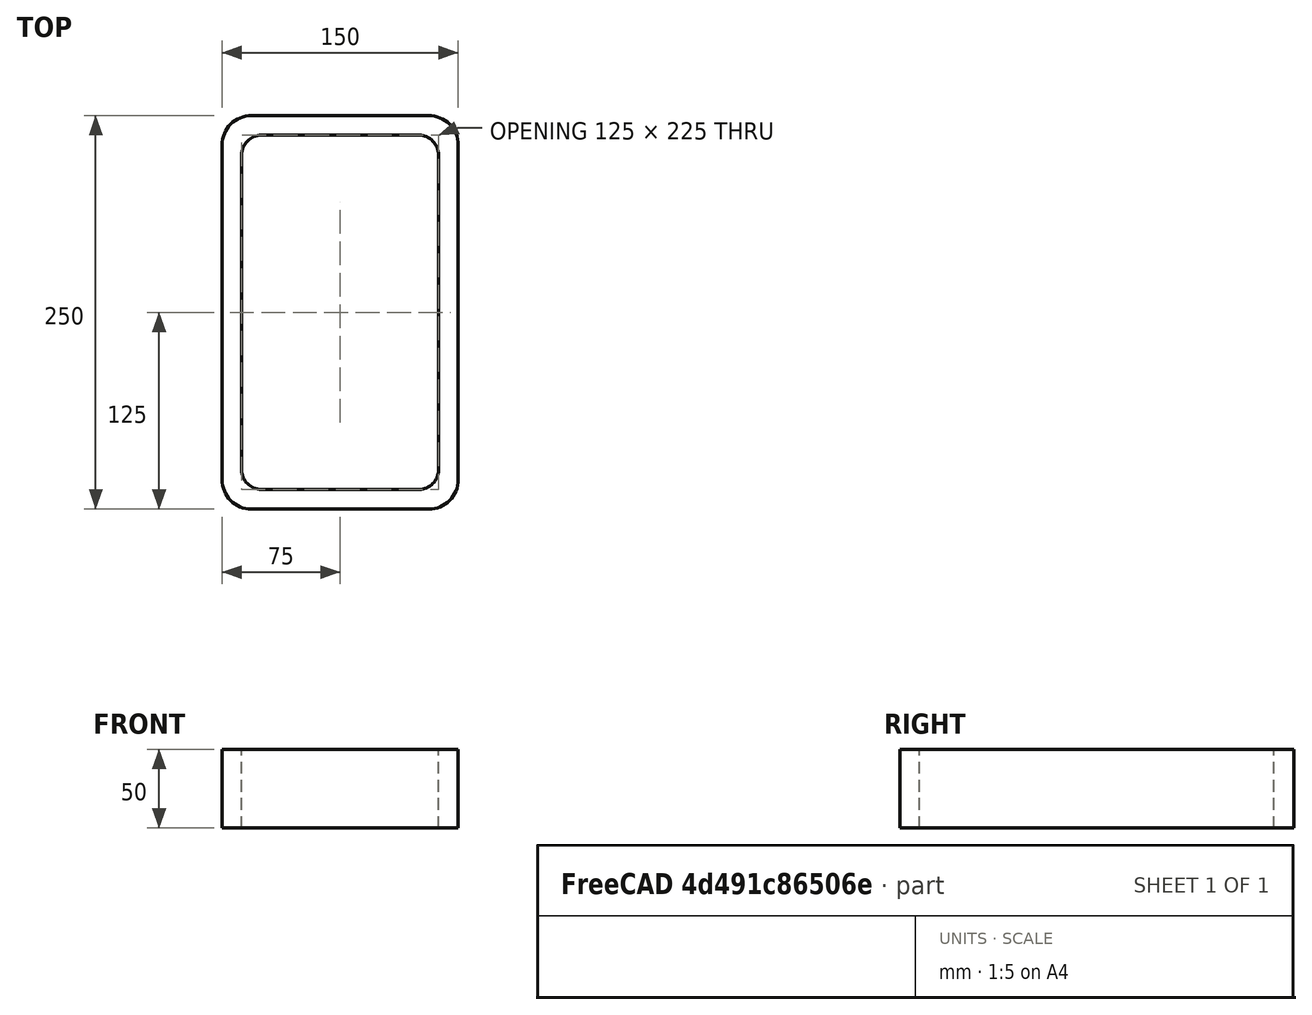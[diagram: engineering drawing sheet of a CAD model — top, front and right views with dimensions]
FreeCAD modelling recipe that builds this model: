
FCSTD DOCUMENT  (FreeCAD 0.15R4671 (Git))
Label: Rectangular hollow section 250x150x12.5 EN10219 S235JRH
License: All rights reserved
LicenseURL: http://en.wikipedia.org/wiki/All_rights_reserved
objects: Sketcher::SketchObject×1, Part::Extrusion×1
note: 2 computed .brp shape members not serialized (recipe doc carries the construction recipe); baked Part::Feature solids carry a one-line shape summary decoded from their .brp

FEATURE [Sketcher::SketchObject] Sketch
  sketch-geometry (16):
    g0: LineSegment StartX=-50 StartY=112.5 StartZ=0 EndX=50 EndY=112.5 EndZ=0
    g1: LineSegment StartX=62.5 StartY=100 StartZ=0 EndX=62.5 EndY=-100 EndZ=0
    g2: LineSegment StartX=50 StartY=-112.5 StartZ=0 EndX=-50 EndY=-112.5 EndZ=0
    g3: LineSegment StartX=-62.5 StartY=-100 StartZ=0 EndX=-62.5 EndY=100 EndZ=0
    g4: LineSegment StartX=-56.25 StartY=125 StartZ=0 EndX=56.25 EndY=125 EndZ=0
    g5: LineSegment StartX=75 StartY=106.25 StartZ=0 EndX=75 EndY=-106.25 EndZ=0
    g6: LineSegment StartX=56.25 StartY=-125 StartZ=0 EndX=-56.25 EndY=-125 EndZ=0
    g7: LineSegment StartX=-75 StartY=-106.25 StartZ=0 EndX=-75 EndY=106.25 EndZ=0
    g8: ArcOfCircle CenterX=-50 CenterY=100 CenterZ=0 NormalX=0 NormalY=0 NormalZ=1 Radius=12.5 StartAngle=1.5708 EndAngle=3.14159
    g9: ArcOfCircle CenterX=50 CenterY=100 CenterZ=0 NormalX=0 NormalY=0 NormalZ=1 Radius=12.5 StartAngle=0 EndAngle=1.5708
    g10: ArcOfCircle CenterX=50 CenterY=-100 CenterZ=0 NormalX=0 NormalY=0 NormalZ=1 Radius=12.5 StartAngle=4.71239 EndAngle=6.28319
    g11: ArcOfCircle CenterX=-50 CenterY=-100 CenterZ=0 NormalX=0 NormalY=0 NormalZ=1 Radius=12.5 StartAngle=3.14159 EndAngle=4.71239
    g12: ArcOfCircle CenterX=56.25 CenterY=106.25 CenterZ=0 NormalX=0 NormalY=0 NormalZ=1 Radius=18.75 StartAngle=0 EndAngle=1.5708
    g13: ArcOfCircle CenterX=56.25 CenterY=-106.25 CenterZ=0 NormalX=0 NormalY=0 NormalZ=1 Radius=18.75 StartAngle=4.71239 EndAngle=6.28319
    g14: ArcOfCircle CenterX=-56.25 CenterY=-106.25 CenterZ=0 NormalX=0 NormalY=0 NormalZ=1 Radius=18.75 StartAngle=3.14159 EndAngle=4.71239
    g15: ArcOfCircle CenterX=-56.25 CenterY=106.25 CenterZ=0 NormalX=0 NormalY=0 NormalZ=1 Radius=18.75 StartAngle=1.5708 EndAngle=3.14159
  constraints (36):
    c: Horizontal(g2)
    c: Vertical(g3)
    c: Horizontal(g6)
    c: Vertical(g7)
    c: Tangent(g3,g8) = 1.5708
    c: Tangent(g0,g8) = 1.5708
    c: Tangent(g0,g9) = 1.5708
    c: Tangent(g1,g9) = 1.5708
    c: Tangent(g1,g10) = 1.5708
    c: Tangent(g2,g10) = 1.5708
    c: Tangent(g2,g11) = 1.5708
    c: Tangent(g3,g11) = 1.5708
    c: Tangent(g4,g12) = 1.5708
    c: Tangent(g5,g12) = 1.5708
    c: Tangent(g5,g13) = 1.5708
    c: Tangent(g6,g13) = 1.5708
    c: Tangent(g6,g14) = 1.5708
    c: Tangent(g7,g14) = 1.5708
    c: Tangent(g7,g15) = 1.5708
    c: Tangent(g4,g15) = 1.5708
    c: Equal(g9,g8)
    c: Equal(g9,g11)
    c: Equal(g9,g10)
    c: Equal(g12,g15)
    c: Equal(g12,g14)
    c: Equal(g12,g13)
    c: Symmetric(g4,g6,g-1)
    c: Symmetric(g7,g5,g-2)
    c: DistanceY(g4,g6) = -250
    c: DistanceX(g7,g5) = 150
    c: Symmetric(g3,g1,g-2)
    c: Symmetric(g0,g2,g-1)
    c: DistanceY(g0,g4) = 12.5
    c: DistanceX(g5,g1) = -12.5
    c: Radius(g9) = 12.5
    c: Radius(g12) = 18.75
FEATURE [Part::Extrusion] Extrude  label="Rectangular hollow section 250x150x12.5 EN10219 S235JRH"
  Base = -> Sketch
  Dir = (0,0,50)
  Solid = true
